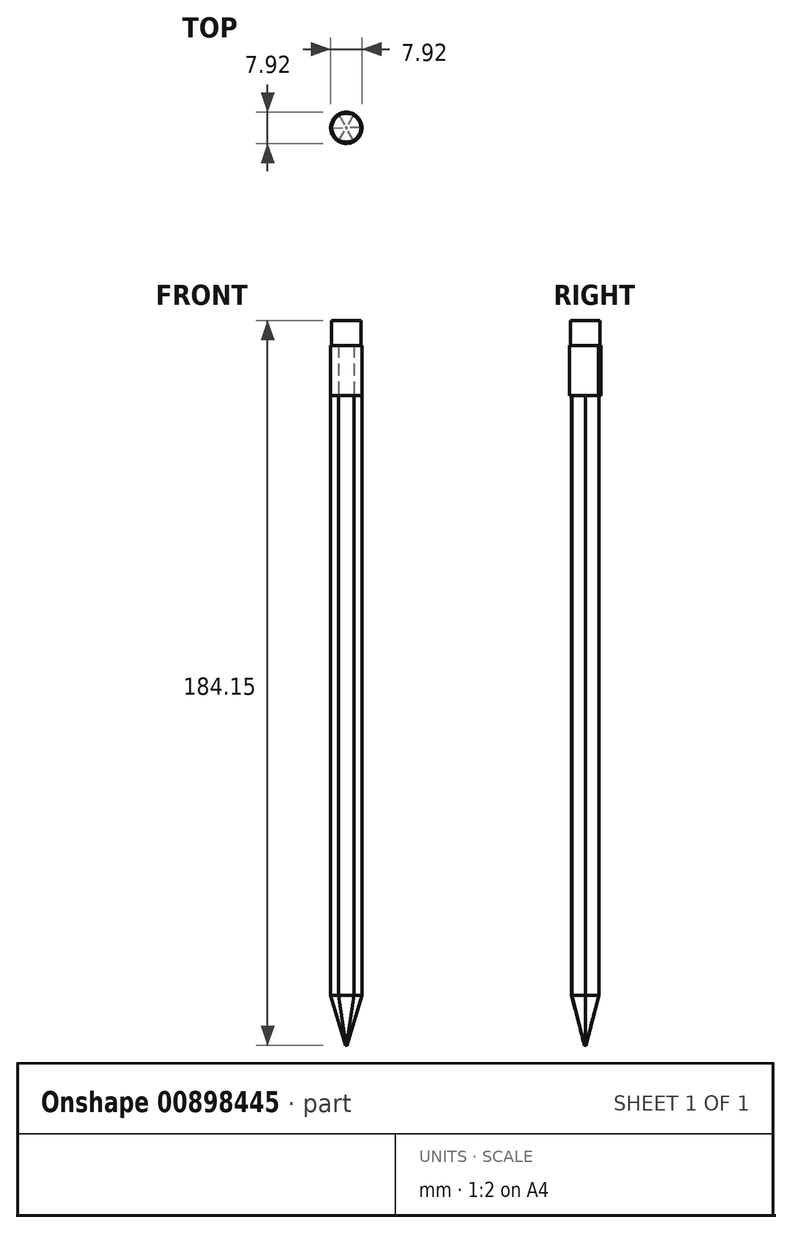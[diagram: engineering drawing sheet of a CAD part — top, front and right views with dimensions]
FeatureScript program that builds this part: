
annotation { "Feature Type Name" : "Feature", "Feature Type Description" : "" }
export const myFeature = defineFeature(function(context is Context, id is Id, definition is map)
    precondition{}
    {
        {
            var Q0;
            Q0=qCreatedBy(makeId("Top.planeOp"),FACE);
            var sketch = newSketch(context, id + "F0", { "sketchPlane" : qUnion([Q0])});
            skCircle(sketch, "E0.cCircle", {"center": v(18.56, 13.1) * mm, "radius": 3.43 * mm, "construction": true});
            skLineSegment(sketch, "E0.0", {"start": v(20.5, 16.54) * mm, "end": v(22.52, 13.14) * mm});
            skLineSegment(sketch, "E0.1", {"start": v(22.52, 13.14) * mm, "end": v(20.58, 9.69) * mm});
            skLineSegment(sketch, "E0.2", {"start": v(20.58, 9.69) * mm, "end": v(16.62, 9.65) * mm});
            skLineSegment(sketch, "E0.3", {"start": v(16.62, 9.65) * mm, "end": v(14.6, 13.06) * mm});
            skLineSegment(sketch, "E0.4", {"start": v(14.6, 13.06) * mm, "end": v(16.55, 16.5) * mm});
            skLineSegment(sketch, "E0.5", {"start": v(16.55, 16.5) * mm, "end": v(20.5, 16.54) * mm});
            skPoint(sketch, "E0.0.midPoint", {"position": v(21.52, 14.84) * mm});
            skSolve(sketch);
        }
        {
            var Q0;
            Q0=makeQuery(id+"F0.imprint","IMPRINT",FACE,{"disambiguationData":[TD([[makeQuery(id+"F0.imprint","IMPRINT",EDGE,{"derivedFrom":sQuery(id+"F0.wireOp",EDGE,"E0.0")}),-1.0]])]});
            extrude(context, id + "F1", {"entities" : qUnion([Q0]), "depth" : 152.4 * mm, "offsetDistance" : 25.4 * mm});
        }
        {
            var Q0;
            Q0=makeQuery(id+"F1.opExtrude","CAP_FACE",FACE,{"disambiguationData":[OSD([sQuery(id+"F0.wireOp",EDGE,"E0.0"),sQuery(id+"F0.wireOp",EDGE,"E0.1"),sQuery(id+"F0.wireOp",EDGE,"E0.2"),sQuery(id+"F0.wireOp",EDGE,"E0.3"),sQuery(id+"F0.wireOp",EDGE,"E0.4"),sQuery(id+"F0.wireOp",EDGE,"E0.5")])],"isStart":false});
            var sketch = newSketch(context, id + "F2", { "sketchPlane" : qUnion([Q0])});
            skCircle(sketch, "E1", {"center": v(18.56, 13.08) * mm, "radius": 3.96 * mm});
            skPoint(sketch, "E1.first.point", {"position": v(14.6, 13.06) * mm});
            skPoint(sketch, "E1.second.point", {"position": v(22.52, 13.14) * mm});
            skPoint(sketch, "E1.third.point", {"position": v(18.28, 9.13) * mm});
            skSolve(sketch);
        }
        {
            var Q0;
            {var subQ0=sQuery(id+"F2.wireOp",EDGE,"E1");var subQ1=makeQuery(id+"F1.opExtrude","CAP_EDGE",EDGE,{"disambiguationData":[OSD([sQuery(id+"F0.wireOp",EDGE,"E0.5")])],"isStart":false});var subQ2=makeQuery(id+"F2.imprint","INTERSECT",VERTEX,{"disambiguationData":[OD(0.0)],"derivedFrom":[subQ1,subQ0]});Q0=makeQuery(id+"F2.imprint","IMPRINT",FACE,{"disambiguationData":[TD([[makeQuery(id+"F2.imprint","IMPRINT",EDGE,{"disambiguationData":[TD([[subQ2,-1.0]])],"derivedFrom":subQ0}),1.0]])]});}
            var Q1;
            {var subQ0=sQuery(id+"F2.wireOp",EDGE,"E1");var subQ1=makeQuery(id+"F1.opExtrude","CAP_EDGE",EDGE,{"disambiguationData":[OSD([sQuery(id+"F0.wireOp",EDGE,"E0.4")])],"isStart":false});var subQ3=makeQuery(id+"F2.imprint","INTERSECT",VERTEX,{"derivedFrom":[subQ1,subQ0]});Q1=makeQuery(id+"F2.imprint","IMPRINT",FACE,{"disambiguationData":[TD([[makeQuery(id+"F2.imprint","IMPRINT",EDGE,{"disambiguationData":[TD([[subQ3,-1.0]])],"derivedFrom":subQ0}),1.0]])]});}
            var Q2;
            {var subQ1=makeQuery(id+"F1.opExtrude","CAP_EDGE",EDGE,{"disambiguationData":[OSD([sQuery(id+"F0.wireOp",EDGE,"E0.1")])],"isStart":false});Q2=makeQuery(id+"F2.imprint","IMPRINT",FACE,{"disambiguationData":[TD([[makeQuery(id+"F2.imprint","IMPRINT",EDGE,{"derivedFrom":subQ1}),1.0]])]});}
            var Q3;
            {var subQ0=sQuery(id+"F2.wireOp",EDGE,"E1");var subQ1=makeQuery(id+"F1.opExtrude","CAP_EDGE",EDGE,{"disambiguationData":[OSD([sQuery(id+"F0.wireOp",EDGE,"E0.0")])],"isStart":false});var subQ3=makeQuery(id+"F2.imprint","INTERSECT",VERTEX,{"derivedFrom":[subQ1,subQ0]});Q3=makeQuery(id+"F2.imprint","IMPRINT",FACE,{"disambiguationData":[TD([[makeQuery(id+"F2.imprint","IMPRINT",EDGE,{"disambiguationData":[TD([[subQ3,1.0]])],"derivedFrom":subQ0}),1.0]])]});}
            var Q4;
            {var subQ5=makeQuery(id+"F1.opExtrude","CAP_EDGE",EDGE,{"disambiguationData":[OSD([sQuery(id+"F0.wireOp",EDGE,"E0.1")])],"isStart":false});Q4=makeQuery(id+"F2.imprint","IMPRINT",FACE,{"disambiguationData":[TD([[makeQuery(id+"F2.imprint","IMPRINT",EDGE,{"derivedFrom":subQ5}),-1.0]])]});}
            var Q5;
            Q5=makeQuery(id+"F1.opExtrude","CAP_FACE",FACE,{"disambiguationData":[OSD([sQuery(id+"F0.wireOp",EDGE,"E0.0"),sQuery(id+"F0.wireOp",EDGE,"E0.1"),sQuery(id+"F0.wireOp",EDGE,"E0.2"),sQuery(id+"F0.wireOp",EDGE,"E0.3"),sQuery(id+"F0.wireOp",EDGE,"E0.4"),sQuery(id+"F0.wireOp",EDGE,"E0.5")])],"isStart":false});
            var Q6;
            Q6=makeQuery(id+"F1.opExtrude","CAP_FACE",FACE,{"disambiguationData":[OSD([sQuery(id+"F0.wireOp",EDGE,"E0.0"),sQuery(id+"F0.wireOp",EDGE,"E0.1"),sQuery(id+"F0.wireOp",EDGE,"E0.2"),sQuery(id+"F0.wireOp",EDGE,"E0.3"),sQuery(id+"F0.wireOp",EDGE,"E0.4"),sQuery(id+"F0.wireOp",EDGE,"E0.5")])],"isStart":true});
            extrude(context, id + "F3", {"entities" : qUnion([Q0, Q1, Q2, Q3, Q4, Q5, Q6]), "operationType" : NewBodyOperationType.ADD, "depth" : 12.7 * mm, "offsetDistance" : 25.4 * mm});
        }
        {
            var Q0;
            {var subQ0=sQuery(id+"F0.wireOp",EDGE,"E0.5");var subQ1=sQuery(id+"F0.wireOp",EDGE,"E0.4");var subQ2=sQuery(id+"F0.wireOp",EDGE,"E0.3");var subQ3=sQuery(id+"F0.wireOp",EDGE,"E0.2");var subQ4=sQuery(id+"F0.wireOp",EDGE,"E0.1");var subQ5=sQuery(id+"F0.wireOp",EDGE,"E0.0");Q0=makeQuery(id+"F3.boolean.opBoolean","MERGE",FACE,{"derivedFrom":[makeQuery(id+"F3.opExtrude","CAP_FACE",FACE,{"disambiguationData":[OSD([subQ5,subQ4,subQ3,subQ2,subQ1,subQ0]),TDD([makeQuery(id+"F1.opExtrude","CAP_FACE",FACE,{"disambiguationData":[OSD([subQ5,subQ4,subQ3,subQ2,subQ1,subQ0])],"isStart":false})])],"isStart":false}),makeQuery(id+"F3.opExtrude","CAP_FACE",FACE,{"disambiguationData":[OSD([sQuery(id+"F2.wireOp",EDGE,"E1")])],"isStart":false})]});}
            var sketch = newSketch(context, id + "F4", { "sketchPlane" : qUnion([Q0])});
            skCircle(sketch, "E2", {"center": v(18.56, 13.08) * mm, "radius": 3.71 * mm});
            skSolve(sketch);
        }
        {
            var Q0;
            Q0=makeQuery(id+"F4.imprint","IMPRINT",FACE,{"disambiguationData":[TD([[makeQuery(id+"F4.imprint","IMPRINT",EDGE,{"derivedFrom":sQuery(id+"F4.wireOp",EDGE,"E2")}),1.0]])]});
            extrude(context, id + "F5", {"entities" : qUnion([Q0]), "operationType" : NewBodyOperationType.ADD, "depth" : 6.35 * mm, "offsetDistance" : 25.4 * mm});
        }
        {
            var Q0;
            Q0=makeQuery(id+"F1.opExtrude","CAP_FACE",FACE,{"disambiguationData":[OSD([sQuery(id+"F0.wireOp",EDGE,"E0.0"),sQuery(id+"F0.wireOp",EDGE,"E0.1"),sQuery(id+"F0.wireOp",EDGE,"E0.2"),sQuery(id+"F0.wireOp",EDGE,"E0.3"),sQuery(id+"F0.wireOp",EDGE,"E0.4"),sQuery(id+"F0.wireOp",EDGE,"E0.5")])],"isStart":true});
            cPlane(context, id + "F6", {"entities" : qUnion([Q0]), "cplaneType" : CPlaneType.OFFSET, "offset" : 12.7 * mm, "width" : 152.4 * mm, "height" : 152.4 * mm});
        }
        {
            var Q0;
            Q0=qCreatedBy(id+"F6.planeOp",FACE);
            var sketch = newSketch(context, id + "F7", { "sketchPlane" : qUnion([Q0])});
            skLineSegment(sketch, "E3.0.0", {"start": v(16.55, -16.5) * mm, "end": v(20.5, -16.54) * mm});
            skLineSegment(sketch, "E3.0.1", {"start": v(20.5, -16.54) * mm, "end": v(22.52, -13.14) * mm});
            skLineSegment(sketch, "E3.0.2", {"start": v(22.52, -13.14) * mm, "end": v(20.58, -9.69) * mm});
            skLineSegment(sketch, "E3.0.3", {"start": v(20.58, -9.69) * mm, "end": v(16.62, -9.65) * mm});
            skLineSegment(sketch, "E3.0.4", {"start": v(16.62, -9.65) * mm, "end": v(14.6, -13.06) * mm});
            skLineSegment(sketch, "E3.0.5", {"start": v(14.6, -13.06) * mm, "end": v(16.55, -16.5) * mm});
            skLineSegment(sketch, "E4", {"start": v(16.62, -9.65) * mm, "end": v(20.5, -16.54) * mm, "construction": true});
            skLineSegment(sketch, "E5", {"start": v(20.58, -9.69) * mm, "end": v(16.55, -16.5) * mm, "construction": true});
            skCircle(sketch, "E6", {"center": v(18.56, -13.1) * mm, "radius": 0.2 * mm});
            skSolve(sketch);
        }
        {
            var Q1;
            Q1=makeQuery(id+"F1.opExtrude","CAP_FACE",FACE,{"disambiguationData":[OSD([sQuery(id+"F0.wireOp",EDGE,"E0.0"),sQuery(id+"F0.wireOp",EDGE,"E0.1"),sQuery(id+"F0.wireOp",EDGE,"E0.2"),sQuery(id+"F0.wireOp",EDGE,"E0.3"),sQuery(id+"F0.wireOp",EDGE,"E0.4"),sQuery(id+"F0.wireOp",EDGE,"E0.5")])],"isStart":true});
            var Q2;
            Q2=makeQuery(id+"F7.imprint","IMPRINT",FACE,{"disambiguationData":[TD([[makeQuery(id+"F7.imprint","IMPRINT",EDGE,{"derivedFrom":sQuery(id+"F7.wireOp",EDGE,"E6")}),1.0]])]});
            loft(context, id + "F8", {"operationType" : NewBodyOperationType.ADD, "sheetProfilesArray" : [{ "sheetProfileEntities" : qUnion([Q1]) }, { "sheetProfileEntities" : qUnion([Q2]) }]});
        }
    });
